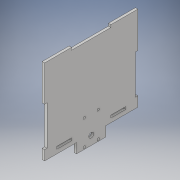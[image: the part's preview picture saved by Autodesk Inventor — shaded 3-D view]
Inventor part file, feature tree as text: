
AUTODESK INVENTOR PART (.ipt)
format: ipt  version: 2019 (Build 230136000, 136)  size: 238,592 bytes
history: native  units: in
note: dims shown in document units (in); Inventor stores cm internally (conversion verified against a paired STEP export)
features: extrude x11, sketch x11
ambient origin geometry x8: Origin, YZ Plane, XZ Plane, XY Plane, X Axis, Y Axis, Z Axis, Center Point
bodies: Solid1 (feature_tree)
feature tree (22):
  extrude  "Extrusion1"  Depth=4.5in
  extrude  "Extrusion2"  Depth=0.125in
  extrude  "Extrusion3"  Depth=0.118in
  extrude  "Extrusion5"  Depth=0.118in
  extrude  "Extrusion6"  Depth=0.1in
  extrude  "Extrusion7"  Depth=0.25in
  extrude  "Extrusion8"  Depth=0.354in
  extrude  "Extrusion9"  Depth=0.125in
  extrude  "Extrusion10"  Depth=1.299in
  extrude  "Extrusion11"  Depth=0.75in
  extrude  "Extrusion12"  Depth=0.125in TaperAngle=0.0deg
  sketch  "Sketch1"  dims[d0=4.5in d1=3.836in]
  sketch  "Sketch2"  dims[d2=0.125in d3=0.0in d4=0.709in]
  sketch  "Sketch3"  dims[d5=0.118in d6=0.118in]
  sketch  "Sketch4"  dims[d7=0.118in d8=0.118in]
  sketch  "Sketch5"  dims[d11=0.709in d12=0.1in]
  sketch  "Sketch6"  dims[d13=0.125in d14=0.0in d15=0.25in]
  sketch  "Sketch7"  dims[d16=2.25in d17=0.354in]
  sketch  "Sketch8"  dims[d18=0.125in d19=0.0in d28=0.1in]
  sketch  "Sketch9"  dims[d29=1.299in d30=1.299in]
  sketch  "Sketch10"  dims[d31=0.125in d33=0.75in]
  sketch  "Sketch11"  dims[d34=0.5in d35=0.125in d36=0.0in d37=1.5in d38=0.5in d39=1.5in d40=0.125in d41=0.0in d42=0.5in d43=0.711in d44=1.5in d45=0.75in d46=0.125in d47=0.125in d48=0.0in d49=0.125in d50=0.125in d51=0.0in d52=0.125in d53=0.0in d54=0.125in d55=0.125in d56=2.0in d57=2.0in d58=0.5in d59=0.125in d60=0.0in d61=0.125in d62=0.0in d65=1.8955in d66=0.0in d67=1.0in d68=0.125in d69=0.0in d70=2.0in d71=0.125in d72=1.375in d73=0.125in d74=0.0in]
